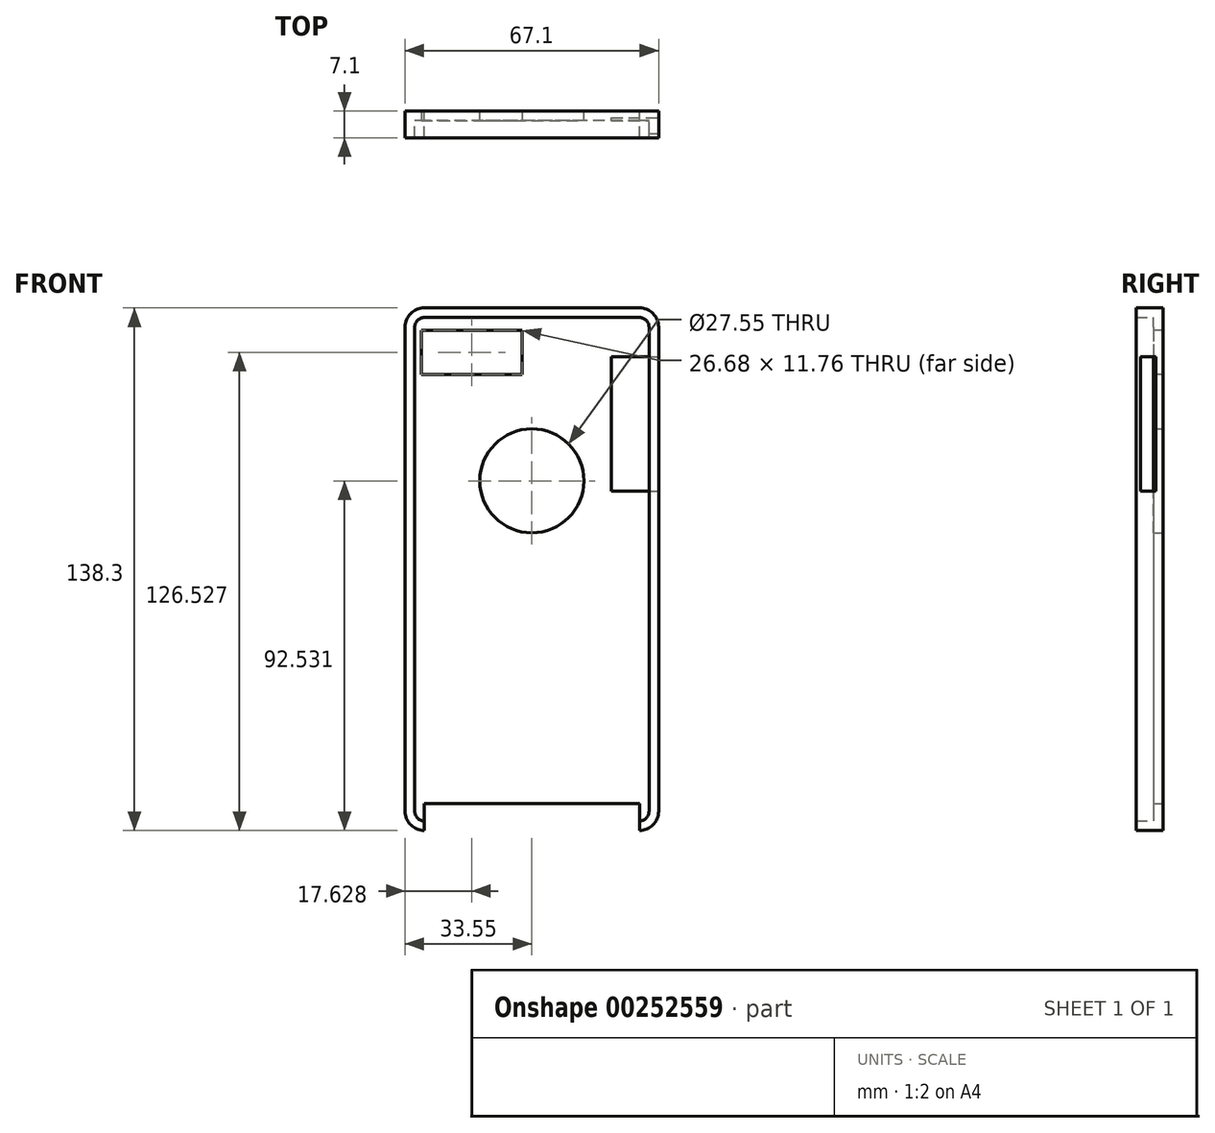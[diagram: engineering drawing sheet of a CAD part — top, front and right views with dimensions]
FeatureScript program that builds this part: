
annotation { "Feature Type Name" : "Feature", "Feature Type Description" : "" }
export const myFeature = defineFeature(function(context is Context, id is Id, definition is map)
    precondition{}
    {
        {
            var Q0;
            Q0=qCreatedBy(makeId("Front.planeOp"),FACE);
            var sketch = newSketch(context, id + "F0", { "sketchPlane" : qUnion([Q0])});
            skLineSegment(sketch, "E0.bottom", {"start": v(33.55, 69.15) * mm, "end": v(-33.55, 69.15) * mm});
            skLineSegment(sketch, "E0.top", {"start": v(33.55, -69.15) * mm, "end": v(-33.55, -69.15) * mm});
            skLineSegment(sketch, "E0.left", {"start": v(33.55, 69.15) * mm, "end": v(33.55, -69.15) * mm});
            skLineSegment(sketch, "E0.right", {"start": v(-33.55, 69.15) * mm, "end": v(-33.55, -69.15) * mm});
            skPoint(sketch, "E0.middle", {"position": v(0, 0) * mm});
            skSolve(sketch);
        }
        {
            var Q0;
            Q0=makeQuery(id+"F0.imprint","IMPRINT",FACE,{"disambiguationData":[TD([[makeQuery(id+"F0.imprint","IMPRINT",EDGE,{"derivedFrom":sQuery(id+"F0.wireOp",EDGE,"E0.bottom")}),1.0]])]});
            extrude(context, id + "F1", {"entities" : qUnion([Q0]), "endBound" : BoundingType.SYMMETRIC, "depth" : 7.1 * mm});
        }
        {
            var Q0;
            Q0=makeQuery(id+"F1.opExtrude","SWEPT_EDGE",EDGE,{"disambiguationData":[OSD([sQuery(id+"F0.wireOp",EDGE,"E0.bottom"),sQuery(id+"F0.wireOp",EDGE,"E0.left")])]});
            var Q1;
            Q1=makeQuery(id+"F1.opExtrude","SWEPT_EDGE",EDGE,{"disambiguationData":[OSD([sQuery(id+"F0.wireOp",EDGE,"E0.bottom"),sQuery(id+"F0.wireOp",EDGE,"E0.right")])]});
            var Q2;
            Q2=makeQuery(id+"F1.opExtrude","SWEPT_EDGE",EDGE,{"disambiguationData":[OSD([sQuery(id+"F0.wireOp",EDGE,"E0.top"),sQuery(id+"F0.wireOp",EDGE,"E0.right")])]});
            var Q3;
            Q3=makeQuery(id+"F1.opExtrude","SWEPT_EDGE",EDGE,{"disambiguationData":[OSD([sQuery(id+"F0.wireOp",EDGE,"E0.top"),sQuery(id+"F0.wireOp",EDGE,"E0.left")])]});
            fillet(context, id + "F2", {"entities" : qUnion([Q0, Q1, Q2, Q3]), "radius" : 5.08 * mm, "tangentPropagation" : true, "allowEdgeOverflow" : false});
        }
        {
            var Q0;
            Q0=makeQuery(id+"F1.opExtrude","CAP_FACE",FACE,{"disambiguationData":[OSD([sQuery(id+"F0.wireOp",EDGE,"E0.bottom"),sQuery(id+"F0.wireOp",EDGE,"E0.top"),sQuery(id+"F0.wireOp",EDGE,"E0.left"),sQuery(id+"F0.wireOp",EDGE,"E0.right")])],"isStart":false});
            shell(context, id + "F3", {"entities" : qUnion([Q0]), "thickness" : 2.54 * mm});
        }
        {
            var Q0;
            Q0=makeQuery(id+"F1.opExtrude","SWEPT_FACE",FACE,{"disambiguationData":[OSD([sQuery(id+"F0.wireOp",EDGE,"E0.top")])]});
            extrude(context, id + "F4", {"entities" : qUnion([Q0]), "operationType" : NewBodyOperationType.REMOVE, "oppositeDirection" : true, "depth" : 7.1 * mm});
        }
        {
            var Q0;
            Q0=qCreatedBy(makeId("Front.planeOp"),FACE);
            var sketch = newSketch(context, id + "F5", { "sketchPlane" : qUnion([Q0])});
            skLineSegment(sketch, "E1.bottom", {"start": v(-29.26, 63.26) * mm, "end": v(-2.58, 63.26) * mm});
            skLineSegment(sketch, "E1.top", {"start": v(-29.26, 51.5) * mm, "end": v(-2.58, 51.5) * mm});
            skLineSegment(sketch, "E1.left", {"start": v(-29.26, 63.26) * mm, "end": v(-29.26, 51.5) * mm});
            skLineSegment(sketch, "E1.right", {"start": v(-2.58, 63.26) * mm, "end": v(-2.58, 51.5) * mm});
            skSolve(sketch);
        }
        {
            var Q0;
            Q0=makeQuery(id+"F5.imprint","IMPRINT",FACE,{"disambiguationData":[TD([[makeQuery(id+"F5.imprint","IMPRINT",EDGE,{"derivedFrom":sQuery(id+"F5.wireOp",EDGE,"E1.bottom")}),-1.0]])]});
            extrude(context, id + "F6", {"entities" : qUnion([Q0]), "operationType" : NewBodyOperationType.REMOVE, "oppositeDirection" : true, "depth" : 25 * mm});
        }
        {
            var Q0;
            Q0=makeQuery(id+"F1.opExtrude","CAP_FACE",FACE,{"disambiguationData":[OSD([sQuery(id+"F0.wireOp",EDGE,"E0.bottom"),sQuery(id+"F0.wireOp",EDGE,"E0.top"),sQuery(id+"F0.wireOp",EDGE,"E0.left"),sQuery(id+"F0.wireOp",EDGE,"E0.right")])],"isStart":true});
            var sketch = newSketch(context, id + "F7", { "sketchPlane" : qUnion([Q0])});
            skCircle(sketch, "E2", {"center": v(0, 23.38) * mm, "radius": 13.77 * mm});
            skSolve(sketch);
        }
        {
            var Q0;
            Q0=makeQuery(id+"F7.imprint","IMPRINT",FACE,{"disambiguationData":[TD([[makeQuery(id+"F7.imprint","IMPRINT",EDGE,{"derivedFrom":sQuery(id+"F7.wireOp",EDGE,"E2")}),1.0]])]});
            extrude(context, id + "F8", {"entities" : qUnion([Q0]), "operationType" : NewBodyOperationType.REMOVE, "endBound" : BoundingType.SYMMETRIC, "oppositeDirection" : true, "depth" : 25 * mm});
        }
        {
            var Q0;
            Q0=makeQuery(id+"F1.opExtrude","SWEPT_FACE",FACE,{"disambiguationData":[OSD([sQuery(id+"F0.wireOp",EDGE,"E0.left")])]});
            var sketch = newSketch(context, id + "F9", { "sketchPlane" : qUnion([Q0])});
            skLineSegment(sketch, "E3.bottom", {"start": v(-2.4, 56.2) * mm, "end": v(1.72, 56.2) * mm});
            skLineSegment(sketch, "E3.top", {"start": v(-2.4, 20.65) * mm, "end": v(1.72, 20.65) * mm});
            skLineSegment(sketch, "E3.left", {"start": v(-2.4, 56.2) * mm, "end": v(-2.4, 20.65) * mm});
            skLineSegment(sketch, "E3.right", {"start": v(1.72, 56.2) * mm, "end": v(1.72, 20.65) * mm});
            skSolve(sketch);
        }
        {
            var Q0;
            Q0=makeQuery(id+"F9.imprint","IMPRINT",FACE,{"disambiguationData":[TD([[makeQuery(id+"F9.imprint","IMPRINT",EDGE,{"derivedFrom":sQuery(id+"F9.wireOp",EDGE,"E3.bottom")}),-1.0]])]});
            extrude(context, id + "F10", {"entities" : qUnion([Q0]), "operationType" : NewBodyOperationType.REMOVE, "endBound" : BoundingType.SYMMETRIC, "oppositeDirection" : true, "depth" : 25 * mm});
        }
    });
